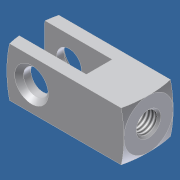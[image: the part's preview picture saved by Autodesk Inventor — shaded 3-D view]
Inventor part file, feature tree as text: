
AUTODESK INVENTOR PART (.ipt)
format: ipt  version: 2012 (Build 160160000, 160)  size: 169,472 bytes
history: native  units: in
note: dims shown in document units (in); Inventor stores cm internally (conversion verified against a paired STEP export)
features: other x126, sketch x7, revolve x5, extrude x2, thread x1
ambient origin geometry x8: Origin, YZ Plane, XZ Plane, XY Plane, X Axis, Y Axis, Z Axis, Center Point
bodies: Solid1 (feature_tree)
feature tree (141):
  extrude  "Extrusion1"  Depth=0.5in TaperAngle=0.0deg
  extrude  "Extrusion2"  Depth=0.44in TaperAngle=0.0deg
  revolve  "Revolution1"  Angle=360.0deg
  thread  "Thread1"  [1 undecoded]
  revolve  "Revolution2"  [1 undecoded]
  revolve  "Revolution3"  [1 undecoded]
  revolve  "Revolution4"  [1 undecoded]
  revolve  "Revolution5"  [1 undecoded]
  other  "th1_XY"
  other  "th1_YZ"
  other  "th1_ZX"
  other  "th1_X"
  other  "th1_Y"
  other  "th1_Z"
  other  "th1_Center"
  other  "th2_XY"
  other  "th2_YZ"
  other  "th2_ZX"
  other  "th2_X"
  other  "th2_Y"
  other  "th2_Z"
  other  "th2_Center"
  other  "rod_clevis_body_XY"
  other  "rod_clevis_body_YZ"
  other  "rod_clevis_body_ZX"
  other  "rod_clevis_body_X"
  other  "rod_clevis_body_Y"
  other  "rod_clevis_body_Z"
  other  "rod_clevis_body_Center"
  other  "piston_rod_clevis_XY"
  other  "piston_rod_clevis_YZ"
  other  "piston_rod_clevis_ZX"
  other  "piston_rod_clevis_X"
  other  "piston_rod_clevis_Y"
  other  "piston_rod_clevis_Z"
  other  "piston_rod_clevis_Center"
  other  "dummy_XY"
  other  "dummy_YZ"
  other  "dummy_ZX"
  other  "dummy_X"
  other  "dummy_Y"
  other  "dummy_Z"
  other  "dummy_Center"
  other  "l11_XY"
  other  "l11_YZ"
  other  "l11_ZX"
  other  "l11_X"
  other  "l11_Y"
  other  "l11_Z"
  other  "l11_Center"
  other  "l12_XY"
  other  "l12_YZ"
  other  "l12_ZX"
  other  "l12_X"
  other  "l12_Y"
  other  "l12_Z"
  other  "l12_Center"
  other  "l1_XY"
  other  "l1_YZ"
  other  "l1_ZX"
  other  "l1_X"
  other  "l1_Y"
  other  "l1_Z"
  other  "l1_Center"
  other  "h1_XY"
  other  "h1_YZ"
  other  "h1_ZX"
  other  "h1_X"
  other  "h1_Y"
  other  "h1_Z"
  other  "h1_Center"
  other  "l2_XY"
  other  "l2_YZ"
  other  "l2_ZX"
  other  "l2_X"
  other  "l2_Y"
  other  "l2_Z"
  other  "l2_Center"
  other  "h2_XY"
  other  "h2_YZ"
  other  "h2_ZX"
  other  "h2_X"
  other  "h2_Y"
  other  "h2_Z"
  other  "h2_Center"
  other  "w11_XY"
  other  "w11_YZ"
  other  "w11_ZX"
  other  "w11_X"
  other  "w11_Y"
  other  "w11_Z"
  other  "w11_Center"
  other  "w12_XY"
  other  "w12_YZ"
  other  "w12_ZX"
  other  "w12_X"
  other  "w12_Y"
  other  "w12_Z"
  other  "w12_Center"
  other  "l21_XY"
  other  "l21_YZ"
  other  "l21_ZX"
  other  "l21_X"
  other  "l21_Y"
  other  "l21_Z"
  other  "l21_Center"
  other  "l22_XY"
  other  "l22_YZ"
  other  "l22_ZX"
  other  "l22_X"
  other  "l22_Y"
  other  "l22_Z"
  other  "l22_Center"
  other  "w1_XY"
  other  "w1_YZ"
  other  "w1_ZX"
  other  "w1_X"
  other  "w1_Y"
  other  "w1_Z"
  other  "w1_Center"
  other  "w2_XY"
  other  "w2_YZ"
  other  "w2_ZX"
  other  "w2_X"
  other  "w2_Y"
  other  "w2_Z"
  other  "w2_Center"
  other  "to_cylinder_XY"
  other  "to_cylinder_YZ"
  other  "to_cylinder_ZX"
  other  "to_cylinder_X"
  other  "to_cylinder_Y"
  other  "to_cylinder_Z"
  other  "to_cylinder_Center"
  sketch  "Sketch_1"  dims[d0=0.5in d1=0.0in d2=0.5in d3=0.0in]
  sketch  "Sketch_2"  dims[d4=360.0deg d5=0.44in d6=0.0in]
  sketch  "Sketch_3"  dims[d7=360.0deg d8=360.0deg d9=360.0deg]
  sketch  "Sketch_4"  dims[d10=360.0deg]
  sketch  "Sketch_5"
  sketch  "Sketch_9"
  sketch  "Sketch_10"
note: 5 required parameter values undecoded (feature->parameter linkage not recoverable at this tier; creation-order binding heuristic only, values carry confidence <= 0.55)
